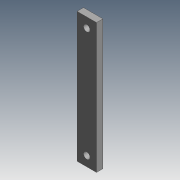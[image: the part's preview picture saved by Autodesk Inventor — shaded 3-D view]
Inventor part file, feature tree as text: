
AUTODESK INVENTOR PART (.ipt)
format: ipt  version: 2015 (Build 190159000, 159)  size: 78,336 bytes
history: native  units: mm
features: extrude x1, sketch x1
ambient origin geometry x8: Origin, YZ Plane, XZ Plane, XY Plane, X Axis, Y Axis, Z Axis, Center Point
bodies: Solid1 (feature_tree)
feature tree (2):
  extrude  "Extrusion1"  Depth=200.0mm
  sketch  "Sketch1"  dims[d0=30.0mm d1=200.0mm d2=10.0mm d3=10.0mm d4=15.0mm d5=15.0mm d6=10.0mm d7=0.0mm]
